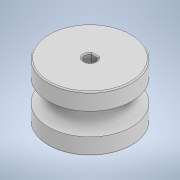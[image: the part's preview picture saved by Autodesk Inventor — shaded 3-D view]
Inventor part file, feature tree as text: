
AUTODESK INVENTOR PART (.ipt)
format: ipt  version: 2021 (Build 250183000, 183)  size: 219,136 bytes
history: native  units: in
note: dims shown in document units (in); Inventor stores cm internally (conversion verified against a paired STEP export)
features: sketch x4, extrude x3, fillet x2, revolve x1, mirror x1
ambient origin geometry x8: Origin, YZ Plane, XZ Plane, XY Plane, X Axis, Y Axis, Z Axis, Center Point
bodies: Solid1 (feature_tree)
feature tree (11):
  revolve  "Revolution1"  [1 undecoded]
  mirror  "Mirror1"
  fillet  "Fillet1"  Radius=0.0591in
  extrude  "Extrusion1"  TaperAngle=90.0deg  [1 undecoded]
  extrude  "Extrusion2"  Depth=0.0197in
  extrude  "Extrusion3"  Depth=0.0197in TaperAngle=0.0deg
  fillet  "Fillet2"  Radius=0.315in
  sketch  "Sketch1"  dims[d0=0.7087in d1=0.4724in d3=0.0591in]
  sketch  "Sketch2"  dims[d4=0.1969in d5=90.0deg]
  sketch  "Sketch3"  dims[d6=0.0197in d7=0.1969in]
  sketch  "Sketch4"  dims[d8=0.0787in d9=0.4823in d10=0.0in d11=0.315in d12=0.4626in d13=0.0in d14=0.5118in d15=0.2756in d16=0.0in d17=0.0197in]
note: 2 required parameter values undecoded (feature->parameter linkage not recoverable at this tier; creation-order binding heuristic only, values carry confidence <= 0.55)